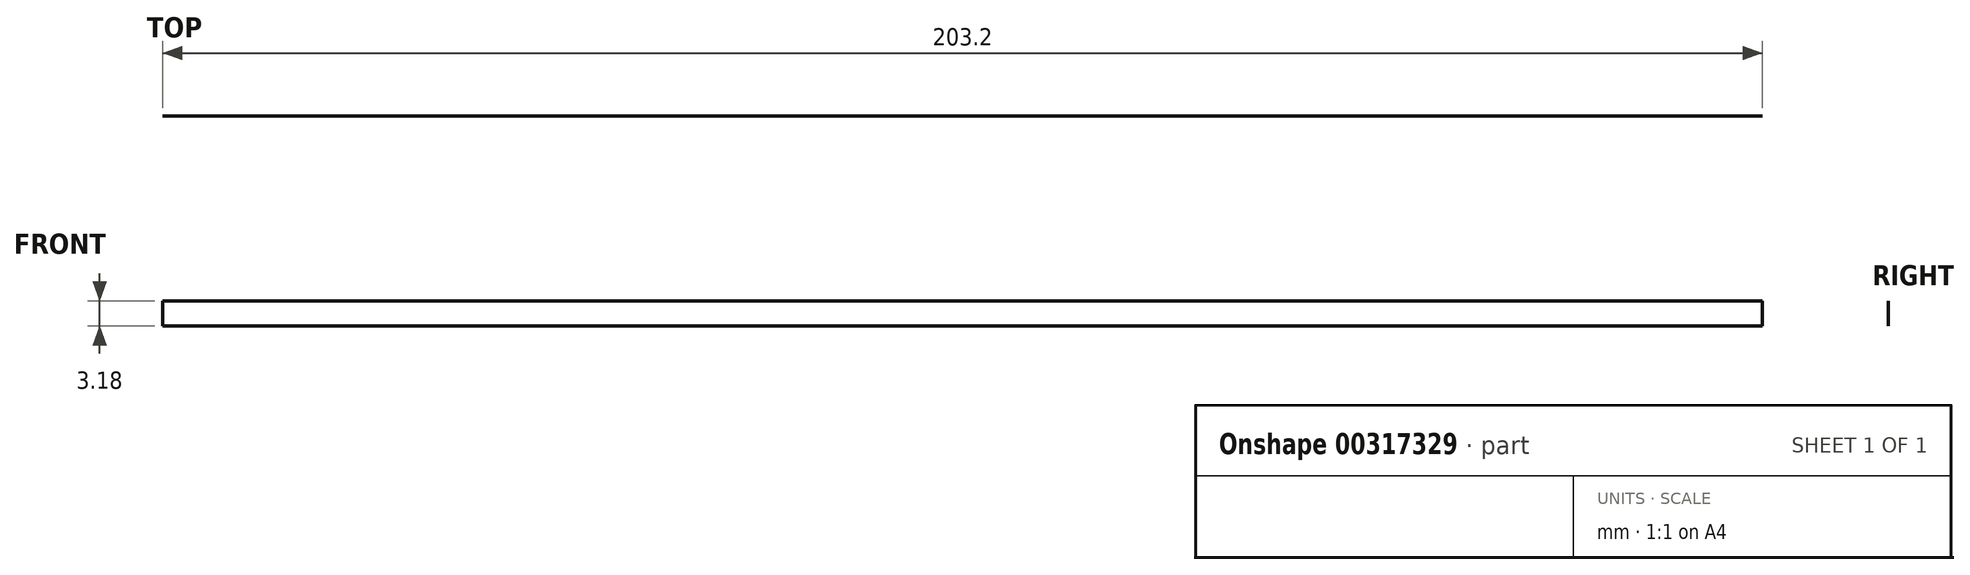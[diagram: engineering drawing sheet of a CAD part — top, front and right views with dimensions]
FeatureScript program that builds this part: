
annotation { "Feature Type Name" : "Feature", "Feature Type Description" : "" }
export const myFeature = defineFeature(function(context is Context, id is Id, definition is map)
    precondition{}
    {
        {
            var Q0;
            Q0=qCreatedBy(makeId("Front.planeOp"),FACE);
            var sketch = newSketch(context, id + "F0", { "sketchPlane" : qUnion([Q0])});
            skLineSegment(sketch, "E0.bottom", {"start": v(-105.05, -7.02) * mm, "end": v(98.15, -7.02) * mm});
            skLineSegment(sketch, "E0.top", {"start": v(-105.05, -10.2) * mm, "end": v(98.15, -10.2) * mm});
            skLineSegment(sketch, "E0.left", {"start": v(-105.05, -7.02) * mm, "end": v(-105.05, -10.2) * mm});
            skLineSegment(sketch, "E0.right", {"start": v(98.15, -7.02) * mm, "end": v(98.15, -10.2) * mm});
            skPoint(sketch, "E0.middle", {"position": v(-3.45, -8.6) * mm});
            skSolve(sketch);
        }
        {
            var Q0;
            Q0 = qSketchRegion(id + "F0", true);
            extrude(context, id + "F1", {"entities" : qUnion([Q0]), "depth" : 1 / 203.2 * mm});
        }
    });
